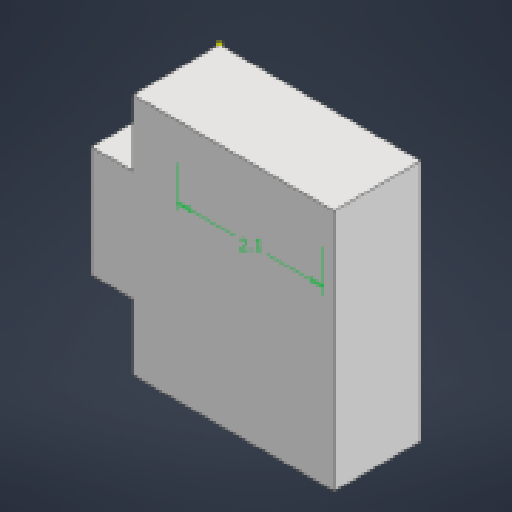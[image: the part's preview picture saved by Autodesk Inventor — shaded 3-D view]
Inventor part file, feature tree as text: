
AUTODESK INVENTOR PART (.ipt)
format: ipt  version: 2023 (Build 270158000, 158)  size: 154,112 bytes
history: native  units: in
note: dims shown in document units (in); Inventor stores cm internally (conversion verified against a paired STEP export)
features: extrude x3, sketch x3
ambient origin geometry x8: Origin, YZ Plane, XZ Plane, XY Plane, X Axis, Y Axis, Z Axis, Center Point
bodies: Solid1 (feature_tree)
feature tree (6):
  extrude  "Extrusion1"  Depth=0.1378in
  extrude  "Extrusion2"  Depth=0.0433in
  extrude  "Extrusion3"  Depth=0.063in
  sketch  "Sketch1"  dims[d0=0.1142in d1=0.1378in]
  sketch  "Sketch2"  dims[d2=0.0492in d3=0.0in d4=0.0433in]
  sketch  "Sketch3"  dims[d5=0.0315in d6=0.063in d7=0.0236in d8=0.0in d9=0.0827in d10=0.0256in d11=0.0256in d12=0.0138in d13=0.0266in d14=0.0276in d15=0.0039in d16=0.0in]
